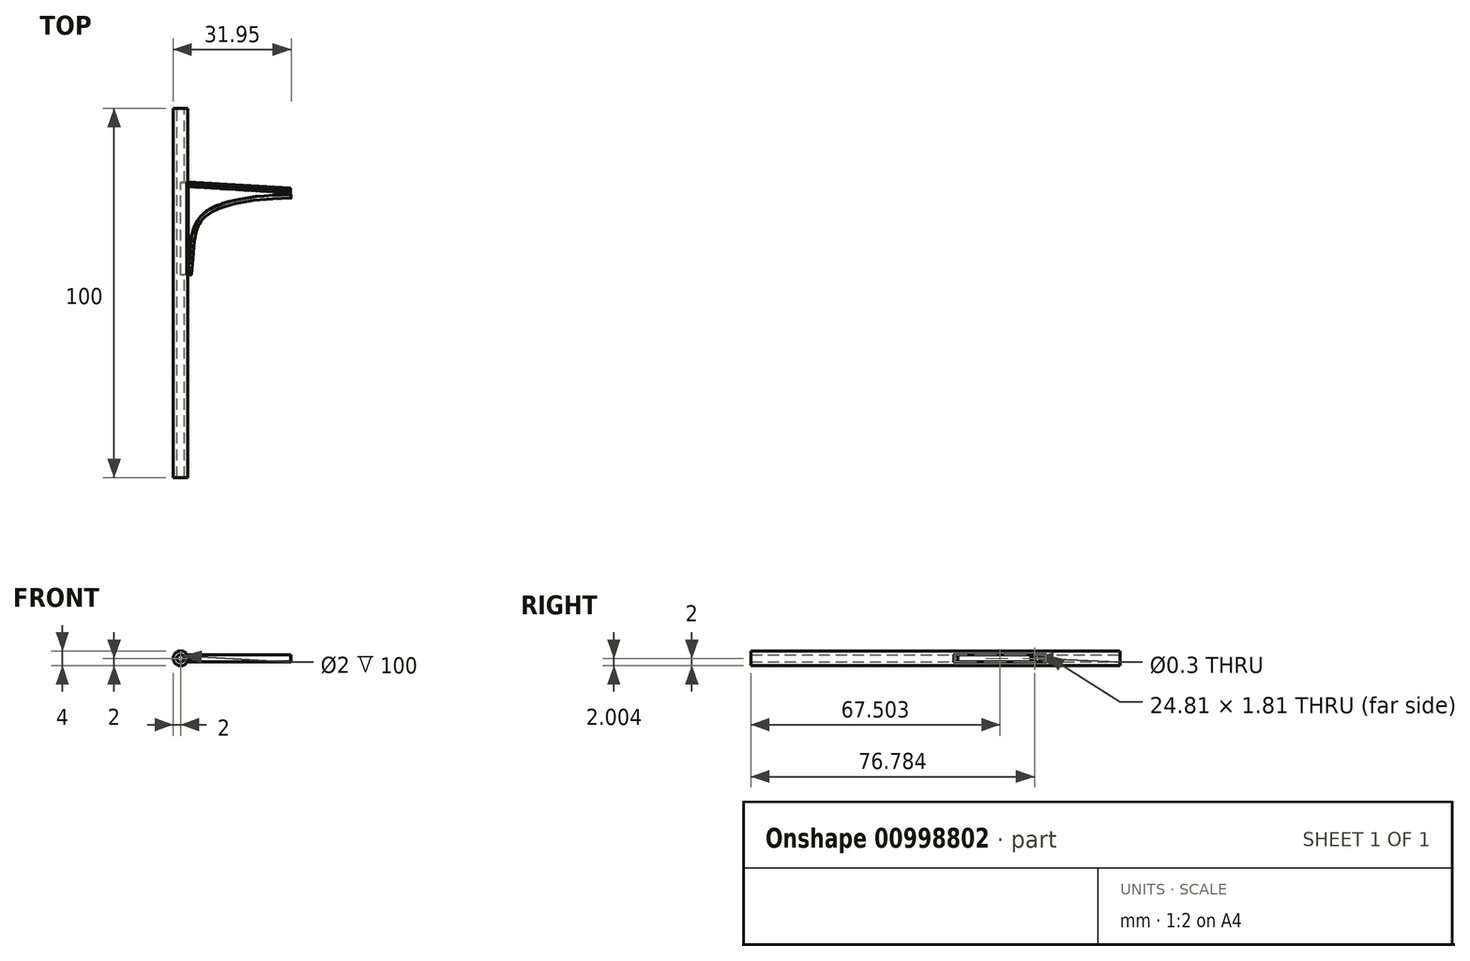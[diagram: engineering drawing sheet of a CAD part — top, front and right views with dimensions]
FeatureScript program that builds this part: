
annotation { "Feature Type Name" : "Feature", "Feature Type Description" : "" }
export const myFeature = defineFeature(function(context is Context, id is Id, definition is map)
    precondition{}
    {
        {
            var Q0;
            Q0=qCreatedBy(makeId("Front.planeOp"),FACE);
            var sketch = newSketch(context, id + "F0", { "sketchPlane" : qUnion([Q0])});
            skCircle(sketch, "E0", {"center": v(0, 0) * mm, "radius": 1 * mm});
            skCircle(sketch, "E1.0", {"center": v(0, 0) * mm, "radius": 2 * mm});
            skPoint(sketch, "E2", {"position": v(0, -1) * mm});
            skSolve(sketch);
        }
        {
            var Q0;
            Q0=qSketchRegion(id+"F0",true);
            extrude(context, id + "F1", {"entities" : qUnion([Q0]), "depth" : 100 * mm, "offsetDistance" : 25 * mm});
        }
        {
            var Q0;
            Q0=sQuery(id+"F0.wireOp",VERTEX,"E2");
            var Q1;
            Q1=sQuery(id+"F0.wireOp",EDGE,"E0");
            cPlane(context, id + "F2", {"entities" : qUnion([Q0, Q1]), "cplaneType" : CPlaneType.LINE_POINT, "offset" : 25 * mm, "width" : 150 * mm, "height" : 150 * mm});
        }
        {
            var Q0;
            Q0=qCreatedBy(id+"F2.planeOp",FACE);
            cPlane(context, id + "F3", {"entities" : qUnion([Q0]), "cplaneType" : CPlaneType.OFFSET, "offset" : 45 * mm, "width" : 150 * mm, "height" : 150 * mm});
        }
        {
            var Q0;
            Q0=qCreatedBy(id+"F3.planeOp",FACE);
            var sketch = newSketch(context, id + "F4", { "sketchPlane" : qUnion([Q0])});
            skLineSegment(sketch, "E3", {"start": v(0, -1) * mm, "end": v(1, -1) * mm, "construction": true});
            skLineSegment(sketch, "E4", {"start": v(0, 1) * mm, "end": v(1, 1) * mm, "construction": true});
            skLineSegment(sketch, "E5", {"start": v(1, -1) * mm, "end": v(1, 1) * mm});
            skSolve(sketch);
        }
        {
            var Q0;
            Q0=qSketchRegion(id+"F4",true);
            var Q1;
            Q1=sQuery(id+"F4.wireOp",EDGE,"E5");
            extrude(context, id + "F5", {"entities" : qUnion([Q0]), "bodyType" : ToolBodyType.SURFACE, "operationType" : NewBodyOperationType.REMOVE, "surfaceEntities" : qUnion([Q1]), "oppositeDirection" : true, "depth" : 25 * mm, "offsetDistance" : 25 * mm});
        }
        {
            var Q0;
            Q0=makeQuery(id+"F5.opExtrude","SWEPT_FACE",FACE,{"disambiguationData":[OSD([sQuery(id+"F4.wireOp",EDGE,"E5")])]});
            extrude(context, id + "F6", {"entities" : qUnion([Q0]), "operationType" : NewBodyOperationType.REMOVE, "oppositeDirection" : true, "depth" : 25 * mm, "offsetDistance" : 25 * mm, "hasSecondDirection" : true, "secondDirectionOppositeDirection" : false, "secondDirectionDepth" : 1 * mm});
        }
        {
            var Q0;
            Q0=makeQuery(id+"F6.boolean.opBoolean","INTERSECT",EDGE,{"derivedFrom":[makeQuery(id+"F1.opExtrude","SWEPT_FACE",FACE,{"disambiguationData":[OSD([sQuery(id+"F0.wireOp",EDGE,"E1.0")])]}),makeQuery(id+"F6.opExtrude","SWEPT_FACE",FACE,{"disambiguationData":[OSD([sQuery(id+"F4.wireOp",VERTEX,"E5.start")])]})]});
            var Q1;
            Q1=makeQuery(id+"F6.boolean.opBoolean","INTERSECT",EDGE,{"derivedFrom":[makeQuery(id+"F1.opExtrude","SWEPT_FACE",FACE,{"disambiguationData":[OSD([sQuery(id+"F0.wireOp",EDGE,"E1.0")])]}),makeQuery(id+"F6.opExtrude","SWEPT_FACE",FACE,{"disambiguationData":[OSD([sQuery(id+"F4.wireOp",VERTEX,"E5.end")])]})]});
            cPlane(context, id + "F7", {"entities" : qUnion([Q0, Q1]), "cplaneType" : CPlaneType.LINE_ANGLE, "offset" : 25 * mm, "angle" : 0 * degree, "width" : 150 * mm, "height" : 150 * mm});
        }
        {
            var Q0;
            Q0=qCreatedBy(id+"F7.planeOp",FACE);
            var sketch = newSketch(context, id + "F8", { "sketchPlane" : qUnion([Q0])});
            skLineSegment(sketch, "E6.bottom", {"start": v(-20, -1) * mm, "end": v(-45, -1) * mm});
            skLineSegment(sketch, "E6.top", {"start": v(-20, 1) * mm, "end": v(-45, 1) * mm});
            skLineSegment(sketch, "E6.left", {"start": v(-20, -1) * mm, "end": v(-20, 1) * mm});
            skLineSegment(sketch, "E6.right", {"start": v(-45, -1) * mm, "end": v(-45, 1) * mm});
            skLineSegment(sketch, "E7", {"start": v(-45, 0) * mm, "end": v(-20, 0) * mm});
            skLineSegment(sketch, "E8", {"start": v(-45, 0) * mm, "end": v(-41.17, 0) * mm});
            skLineSegment(sketch, "E9", {"start": v(-20, 0) * mm, "end": v(-24.2, 0) * mm});
            skSolve(sketch);
        }
        {
            var Q0;
            Q0=qSketchRegion(id+"F8",true);
            extrude(context, id + "F9", {"entities" : qUnion([Q0]), "depth" : 0.3 * mm, "offsetDistance" : 25 * mm});
        }
        {
            var Q0;
            Q0=makeQuery(id+"F9.opExtrude","CAP_FACE",FACE,{"disambiguationData":[OSD([sQuery(id+"F8.wireOp",EDGE,"E6.bottom"),sQuery(id+"F8.wireOp",EDGE,"E6.top"),sQuery(id+"F8.wireOp",EDGE,"E6.left"),sQuery(id+"F8.wireOp",EDGE,"E6.right")])],"isStart":false});
            var Q1;
            Q1=makeQuery(id+"F9.opExtrude","CAP_FACE",FACE,{"disambiguationData":[OSD([sQuery(id+"F8.wireOp",EDGE,"E6.bottom"),sQuery(id+"F8.wireOp",EDGE,"E6.top"),sQuery(id+"F8.wireOp",EDGE,"E6.left"),sQuery(id+"F8.wireOp",EDGE,"E6.right")])],"isStart":true});
            var Q2;
            Q2=makeQuery(id+"F9.opExtrude","SWEPT_BODY",BODY,{"disambiguationData":[OSD([sQuery(id+"F8.wireOp",EDGE,"E6.bottom"),sQuery(id+"F8.wireOp",EDGE,"E6.top"),sQuery(id+"F8.wireOp",EDGE,"E6.left"),sQuery(id+"F8.wireOp",EDGE,"E6.right")])]});
            shell(context, id + "F10", {"entities" : qUnion([Q0, Q1]), "parts" : qUnion([Q2]), "thickness" : 0.1 * mm});
        }
        {
            var Q0;
            Q0=makeQuery(id+"F9.opExtrude","SWEPT_FACE",FACE,{"disambiguationData":[OSD([sQuery(id+"F8.wireOp",EDGE,"E6.top")])]});
            var sketch = newSketch(context, id + "F11", { "sketchPlane" : qUnion([Q0])});
            skSolve(sketch);
        }
        {
            var Q0;
            Q0=sQuery(id+"F8.wireOp",EDGE,"E7");
            cPlane(context, id + "F12", {"entities" : qUnion([Q0]), "cplaneType" : CPlaneType.LINE_ANGLE, "offset" : 25 * mm, "angle" : 0 * degree, "width" : 150 * mm, "height" : 150 * mm});
        }
        {
            var Q0;
            Q0=makeQuery(id+"F9.opExtrude","CAP_FACE",FACE,{"disambiguationData":[OSD([sQuery(id+"F8.wireOp",EDGE,"E6.bottom"),sQuery(id+"F8.wireOp",EDGE,"E6.top"),sQuery(id+"F8.wireOp",EDGE,"E6.left"),sQuery(id+"F8.wireOp",EDGE,"E6.right")])],"isStart":false});
            var sketch = newSketch(context, id + "F13", { "sketchPlane" : qUnion([Q0])});
            skLineSegment(sketch, "E10.bottom", {"start": v(-44.9, -0.9) * mm, "end": v(-20.1, -0.9) * mm});
            skLineSegment(sketch, "E10.top", {"start": v(-44.9, 0.9) * mm, "end": v(-20.1, 0.9) * mm});
            skLineSegment(sketch, "E10.left", {"start": v(-44.9, -0.9) * mm, "end": v(-44.9, 0.9) * mm});
            skLineSegment(sketch, "E10.right", {"start": v(-20.1, -0.9) * mm, "end": v(-20.1, 0.9) * mm});
            skSolve(sketch);
        }
        {
            var Q0;
            Q0=makeQuery(id+"F13.imprint","IMPRINT",FACE,{"disambiguationData":[TD([[makeQuery(id+"F13.imprint","IMPRINT",EDGE,{"derivedFrom":sQuery(id+"F13.wireOp",EDGE,"E10.bottom")}),-1.0]])]});
            extrude(context, id + "F14", {"entities" : qUnion([Q0]), "operationType" : NewBodyOperationType.REMOVE, "oppositeDirection" : true, "depth" : 2 * mm, "offsetDistance" : 25 * mm});
        }
        {
            var Q0;
            Q0=makeQuery(id+"F9.opExtrude","CAP_EDGE",EDGE,{"disambiguationData":[OSD([sQuery(id+"F8.wireOp",EDGE,"E6.right")])],"isStart":false});
            cPlane(context, id + "F15", {"entities" : qUnion([Q0]), "cplaneType" : CPlaneType.LINE_ANGLE, "offset" : 25 * mm, "angle" : 90 * degree, "width" : 150 * mm, "height" : 150 * mm});
        }
        {
            var Q0;
            Q0=qCreatedBy(id+"F15.planeOp",FACE);
            var sketch = newSketch(context, id + "F16", { "sketchPlane" : qUnion([Q0])});
            skArc(sketch, "E11", {"start": v(-2.03, 1) * mm, "mid": v(-2.93, 0) * mm, "end": v(-2.03, -1) * mm});
            skPoint(sketch, "E12", {"position": v(-2.93, 0) * mm});
            skLineSegment(sketch, "E13", {"start": v(-2.03, -1) * mm, "end": v(-2.03, 1) * mm});
            skSolve(sketch);
        }
        {
            var Q0;
            Q0=qCreatedBy(id+"F12.planeOp",FACE);
            var sketch = newSketch(context, id + "F17", { "sketchPlane" : qUnion([Q0])});
            skFitSpline(sketch, "E14", {"points": [v(2.24, -44.99) * mm, v(5.83, -29.16) * mm, v(29.88, -23.58) * mm], "startDerivative": vector(5.62, 52.74) * mm, "endDerivative": vector(56.37, 0.2) * mm});
            skSolve(sketch);
        }
        {
            var Q0;
            Q0=makeQuery(id+"F16.imprint","IMPRINT",FACE,{"disambiguationData":[TD([[makeQuery(id+"F16.imprint","IMPRINT",EDGE,{"derivedFrom":sQuery(id+"F16.wireOp",EDGE,"E11")}),1.0]])]});
            var Q1;
            Q1 = qConstructionFilter(qBodyType(qCreatedBy(id + "F17" ,EDGE), BodyType.WIRE), ConstructionObject.NO);
            sweep(context, id + "F18", {"profiles" : qUnion([Q0]), "path" : qUnion([Q1])});
        }
        {
            var Q0;
            Q0=makeQuery(id+"F18.opSweep","CAP_FACE",FACE,{"disambiguationData":[OSD([sQuery(id+"F16.wireOp",EDGE,"E11"),sQuery(id+"F16.wireOp",EDGE,"WA85A7l2-u0vf-G9TA-IQFj-N9G0mvhgZiK2"),sQuery(id+"F17.wireOp",VERTEX,"E14.start")])],"isStart":true});
            var sketch = newSketch(context, id + "F19", { "sketchPlane" : qUnion([Q0])});
            skLineSegment(sketch, "E15.bottom", {"start": v(2.03, -1) * mm, "end": v(2.66, -1) * mm});
            skLineSegment(sketch, "E15.top", {"start": v(2.03, 1) * mm, "end": v(2.66, 1) * mm});
            skLineSegment(sketch, "E15.left", {"start": v(2.03, -1) * mm, "end": v(2.03, 1) * mm});
            skLineSegment(sketch, "E15.right", {"start": v(2.66, -1) * mm, "end": v(2.66, 1) * mm});
            skSolve(sketch);
        }
        {
            var Q0;
            Q0 = qSketchRegion(id + "F19", true);
            var Q1;
            {var subQ1=sQuery(id+"F17.wireOp",VERTEX,"E14.start");var subQ2=makeQuery(id+"F18.opSweep","CAP_EDGE",EDGE,{"disambiguationData":[OSD([sQuery(id+"F16.wireOp",EDGE,"WA85A7l2-u0vf-G9TA-IQFj-N9G0mvhgZiK2"),subQ1])],"isStart":true});var subQ5=sQuery(id+"F19.wireOp",EDGE,"E15.right");var subQ6=makeQuery(id+"F19.imprint","INTERSECT",VERTEX,{"disambiguationData":[OD(0.0)],"derivedFrom":[subQ2,subQ5]});Q1=makeQuery(id+"F19.imprint","IMPRINT",FACE,{"disambiguationData":[TD([[makeQuery(id+"F19.imprint","IMPRINT",EDGE,{"disambiguationData":[TD([[subQ6,-1.0]])],"derivedFrom":subQ5}),1.0]])]});}
            extrude(context, id + "F20", {"entities" : qUnion([Q0, Q1]), "oppositeDirection" : true, "depth" : 1 * mm, "offsetDistance" : 25 * mm});
        }
        {
            var Q0;
            Q0=makeQuery(id+"F13.imprint","IMPRINT",FACE,{"disambiguationData":[TD([[makeQuery(id+"F13.imprint","IMPRINT",EDGE,{"derivedFrom":sQuery(id+"F13.wireOp",EDGE,"E10.bottom")}),1.0]])]});
            var sketch = newSketch(context, id + "F21", { "sketchPlane" : qUnion([Q0])});
            skLineSegment(sketch, "E16", {"start": v(-21.33, -0.83) * mm, "end": v(-21.33, 0.8) * mm});
            skArc(sketch, "E17", {"start": v(-21.33, -0.83) * mm, "mid": v(-19.86, 0) * mm, "end": v(-21.33, 0.8) * mm});
            skSolve(sketch);
        }
        {
            var Q0;
            Q0=qCreatedBy(id+"F12.planeOp",FACE);
            var sketch = newSketch(context, id + "F22", { "sketchPlane" : qUnion([Q0])});
            skLineSegment(sketch, "E18", {"start": v(2, -20.1) * mm, "end": v(29.74, -21.85) * mm});
            skSolve(sketch);
        }
        {
            var Q0;
            {var subQ0=sQuery(id+"F21.wireOp",EDGE,"E17");var subQ1=sQuery(id+"F21.wireOp",EDGE,"E16");var subQ2=makeQuery(id+"F21.imprint","INTERSECT",VERTEX,{"disambiguationData":[OD(1.0)],"derivedFrom":[subQ1,subQ0]});Q0=makeQuery(id+"F21.imprint","IMPRINT",FACE,{"disambiguationData":[TD([[makeQuery(id+"F21.imprint","IMPRINT",EDGE,{"disambiguationData":[TD([[subQ2,1.0]])],"derivedFrom":subQ1}),-1.0]])]});}
            var Q1;
            {var subQ0=sQuery(id+"F21.wireOp",EDGE,"E17");var subQ1=makeQuery(id+"F13.imprint","IMPRINT",EDGE,{"derivedFrom":makeQuery(id+"F9.opExtrude","CAP_EDGE",EDGE,{"disambiguationData":[OSD([sQuery(id+"F8.wireOp",EDGE,"E6.left")])],"isStart":false})});var subQ2=makeQuery(id+"F21.imprint","INTERSECT",VERTEX,{"disambiguationData":[OD(0.0)],"derivedFrom":[subQ1,subQ0]});Q1=makeQuery(id+"F21.imprint","IMPRINT",FACE,{"disambiguationData":[TD([[makeQuery(id+"F21.imprint","IMPRINT",EDGE,{"disambiguationData":[TD([[subQ2,1.0]])],"derivedFrom":subQ0}),1.0]])]});}
            var Q2;
            {var subQ0=sQuery(id+"F21.wireOp",EDGE,"E17");var subQ1=makeQuery(id+"F13.imprint","IMPRINT",EDGE,{"derivedFrom":makeQuery(id+"F9.opExtrude","CAP_EDGE",EDGE,{"disambiguationData":[OSD([sQuery(id+"F8.wireOp",EDGE,"E6.left")])],"isStart":false})});var subQ2=makeQuery(id+"F21.imprint","INTERSECT",VERTEX,{"disambiguationData":[OD(0.0)],"derivedFrom":[subQ1,subQ0]});Q2=makeQuery(id+"F21.imprint","IMPRINT",FACE,{"disambiguationData":[TD([[makeQuery(id+"F21.imprint","IMPRINT",EDGE,{"disambiguationData":[TD([[subQ2,-1.0]])],"derivedFrom":subQ0}),1.0]])]});}
            var Q3;
            Q3=sQuery(id+"F22.wireOp",EDGE,"E18");
            sweep(context, id + "F23", {"profiles" : qUnion([Q0, Q1, Q2]), "path" : qUnion([Q3])});
        }
        {
            var Q0;
            Q0=makeQuery(id+"F23.opSweep","SWEPT_FACE",FACE,{"disambiguationData":[OSD([sQuery(id+"F13.wireOp",EDGE,"E10.top"),sQuery(id+"F22.wireOp",EDGE,"E18")])]});
            var sketch = newSketch(context, id + "F24", { "sketchPlane" : qUnion([Q0])});
            skLineSegment(sketch, "E19", {"start": v(29.74, -22.87) * mm, "end": v(29.74, -23.41) * mm});
            skLineSegment(sketch, "E20", {"start": v(29.74, -22.87) * mm, "end": v(2, -21.12) * mm});
            skLineSegment(sketch, "E21", {"start": v(2, -21.12) * mm, "end": v(2, -45.08) * mm});
            skFitSpline(sketch, "E22", {"points": [v(29.74, -23.41) * mm, v(5.67, -28.98) * mm, v(2, -45.08) * mm], "startDerivative": vector(-52.95, -3.3) * mm, "endDerivative": vector(-5.2, -39.72) * mm});
            skSolve(sketch);
        }
        {
            var Q0;
            Q0 = qSketchRegion(id + "F24", true);
            extrude(context, id + "F25", {"entities" : qUnion([Q0]), "oppositeDirection" : true, "depth" : 0.1 * mm, "offsetDistance" : 25 * mm});
        }
        {
            var Q0;
            Q0=makeQuery(id+"F25.opExtrude","SWEPT_BODY",BODY,{"disambiguationData":[OSD([sQuery(id+"F24.wireOp",EDGE,"E19"),sQuery(id+"F24.wireOp",EDGE,"E20"),sQuery(id+"F24.wireOp",EDGE,"E21"),sQuery(id+"F24.wireOp",EDGE,"E22")])]});
            var Q1;
            Q1=qCreatedBy(id+"F12.planeOp",FACE);
            mirror(context, id + "F26", {"entities" : qUnion([Q0]), "mirrorPlane" : qUnion([Q1])});
        }
        {
            var Q0;
            Q0=makeQuery(id+"F26.opPattern","COPY",FACE,{"derivedFrom":makeQuery(id+"F25.opExtrude","SWEPT_FACE",FACE,{"disambiguationData":[OSD([sQuery(id+"F24.wireOp",EDGE,"E19")])]}),"instanceName":"1"});
            var sketch = newSketch(context, id + "F27", { "sketchPlane" : qUnion([Q0])});
            skLineSegment(sketch, "E23.bottom", {"start": v(-23.41, -0.8) * mm, "end": v(-23.02, -0.8) * mm});
            skLineSegment(sketch, "E23.top", {"start": v(-23.41, 0.82) * mm, "end": v(-23.02, 0.82) * mm});
            skLineSegment(sketch, "E23.left", {"start": v(-23.41, -0.8) * mm, "end": v(-23.41, 0.82) * mm});
            skLineSegment(sketch, "E23.right", {"start": v(-23.02, -0.8) * mm, "end": v(-23.02, 0.82) * mm});
            skLineSegment(sketch, "E24", {"start": v(-23.22, 0.82) * mm, "end": v(-23.22, 0) * mm});
            skSolve(sketch);
        }
        {
            var Q0;
            Q0 = qSketchRegion(id + "F27", true);
            extrude(context, id + "F28", {"entities" : qUnion([Q0]), "oppositeDirection" : true, "depth" : 0.1 * mm, "offsetDistance" : 25 * mm});
        }
        {
            var Q0;
            Q0=sQuery(id+"F27.wireOp",VERTEX,"E24.end");
            var Q1;
            Q1=makeQuery(id+"F28.opExtrude","SWEPT_BODY",BODY,{"disambiguationData":[OSD([sQuery(id+"F27.wireOp",EDGE,"E23.bottom"),sQuery(id+"F27.wireOp",EDGE,"E23.top"),sQuery(id+"F27.wireOp",EDGE,"E23.left"),sQuery(id+"F27.wireOp",EDGE,"E23.right")])]});
            var Q2;
            Q2=makeQuery(id+"F23.opSweep","SWEPT_BODY",BODY,{"disambiguationData":[OSD([sQuery(id+"F13.wireOp",EDGE,"E10.bottom"),sQuery(id+"F13.wireOp",EDGE,"E10.top"),sQuery(id+"F21.wireOp",EDGE,"E16"),sQuery(id+"F21.wireOp",EDGE,"E17"),sQuery(id+"F22.wireOp",EDGE,"E18")])]});
            var Q3;
            Q3=makeQuery(id+"F18.opSweep","SWEPT_BODY",BODY,{"disambiguationData":[OSD([sQuery(id+"F16.wireOp",EDGE,"E11"),sQuery(id+"F16.wireOp",EDGE,"E13"),sQuery(id+"F17.wireOp",EDGE,"E14")])]});
            var Q4;
            Q4=makeQuery(id+"F1.opExtrude","SWEPT_BODY",BODY,{"disambiguationData":[OSD([sQuery(id+"F0.wireOp",EDGE,"E0"),sQuery(id+"F0.wireOp",EDGE,"E1.0")])]});
            var Q5;
            Q5=makeQuery(id+"F20.opExtrude","SWEPT_BODY",BODY,{"disambiguationData":[OSD([sQuery(id+"F19.wireOp",EDGE,"E15.bottom"),sQuery(id+"F19.wireOp",EDGE,"E15.top"),sQuery(id+"F19.wireOp",EDGE,"E15.left"),sQuery(id+"F19.wireOp",EDGE,"E15.right")])]});
            var Q6;
            Q6=makeQuery(id+"F25.opExtrude","SWEPT_BODY",BODY,{"disambiguationData":[OSD([sQuery(id+"F24.wireOp",EDGE,"E19"),sQuery(id+"F24.wireOp",EDGE,"E20"),sQuery(id+"F24.wireOp",EDGE,"E21"),sQuery(id+"F24.wireOp",EDGE,"E22")])]});
            var Q7;
            Q7=makeQuery(id+"F9.opExtrude","SWEPT_BODY",BODY,{"disambiguationData":[OSD([sQuery(id+"F8.wireOp",EDGE,"E6.bottom"),sQuery(id+"F8.wireOp",EDGE,"E6.top"),sQuery(id+"F8.wireOp",EDGE,"E6.left"),sQuery(id+"F8.wireOp",EDGE,"E6.right")])]});
            var Q8;
            Q8=makeQuery(id+"F26.opPattern","COPY",BODY,{"derivedFrom":makeQuery(id+"F25.opExtrude","SWEPT_BODY",BODY,{"disambiguationData":[OSD([sQuery(id+"F24.wireOp",EDGE,"E19"),sQuery(id+"F24.wireOp",EDGE,"E20"),sQuery(id+"F24.wireOp",EDGE,"E21"),sQuery(id+"F24.wireOp",EDGE,"E22")])]}),"instanceName":"1"});
            hole(context, id + "F29", {"style" : HoleStyle.SIMPLE, "endStyle" : HoleEndStyle.BLIND, "holeDiameter" : 0.3 * mm, "majorDiameter" : 5 * mm, "holeDepth" : 2 * mm, "isTappedThrough" : true, "tappedDepth" : 12 * mm, "tapClearance" : 3, "locations" : qUnion([Q0]), "scope" : qUnion([Q1, Q2, Q3, Q4, Q5, Q6, Q7, Q8])});
        }
    });
